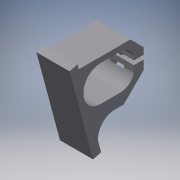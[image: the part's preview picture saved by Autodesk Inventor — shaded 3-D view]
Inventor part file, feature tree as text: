
AUTODESK INVENTOR PART (.ipt)
format: ipt  version: 2018 (Build 220112000, 112)  size: 221,696 bytes
history: native  units: mm
features: reference x19, extrude x7, sketch x7, other x5, thicken_offset x2, chamfer x1
ambient origin geometry x8: Origin, YZ Plane, XZ Plane, XY Plane, X Axis, Y Axis, Z Axis, Center Point
bodies: Solid1 (feature_tree)
feature tree (41):
  extrude  "Extrusion1"  Depth=6.0mm
  extrude  "Extrusion2"  Depth=6.0mm
  chamfer  "Chamfer1"  Distance=12.0mm
  thicken_offset  "Thicken1"
  extrude  "Extrusion4"  Depth=8.0mm
  extrude  "Extrusion6"  Depth=8.0mm TaperAngle=45.0deg
  extrude  "Extrusion7"  Depth=8.0mm TaperAngle=0.0deg
  thicken_offset  "Thicken2"
  extrude  "Extrusion8"  TaperAngle=0.0deg  [1 undecoded]
  extrude  "Extrusion9"  Depth=8.0mm TaperAngle=0.0deg
  sketch  "Sketch1"  dims[d9=20.0mm d10=6.0mm]
  reference  "Reference1"
  reference  "Reference2"
  reference  "Reference3"
  reference  "Reference4"
  reference  "Reference5"
  reference  "Reference6"
  sketch  "Sketch2"  dims[d16=20.0mm d17=6.0mm]
  sketch  "Sketch4"  dims[d18=6.0mm]
  reference  "Reference17"
  reference  "Reference18"
  sketch  "Sketch6"  dims[d19=10.0mm d20=12.0mm d21=0.0mm]
  reference  "Reference23"
  sketch  "Sketch7"  dims[d22=8.0mm d23=6.0mm]
  reference  "Reference24"
  reference  "Reference25"
  reference  "Reference26"
  reference  "Reference27"
  reference  "Reference28"
  reference  "Reference29"
  reference  "Reference30"
  reference  "Reference31"
  reference  "Reference32"
  reference  "Reference33"
  sketch  "Sketch8"  dims[d24=9.0mm d25=0.0mm d27=8.0mm d28=2.0mm d29=45.0deg]
  sketch  "Sketch9"  dims[d32=0.2mm d33=0.2mm d34=9.0mm d35=0.0mm d38=0.0mm d39=0.0mm d40=9.0mm d41=0.0mm d42=0.2mm d43=0.2mm d44=8.0mm d45=25.0mm d46=8.0mm d47=16.5mm d48=9.0mm d49=0.0mm d50=9.0mm d51=0.0mm]
  other  "<userpath>\Dropbox\Skola\Projekt\Kretsn_Brillz_V2\3D\IR_Transmitter.iam"
  other  "IR_Transmitter.iam"
  other  "Powerbank:1"
  other  "IR_PCB_Inventor:1"
  other  "Stand_Back:1"
note: 1 required parameter value undecoded (feature->parameter linkage not recoverable at this tier; creation-order binding heuristic only, values carry confidence <= 0.55)
